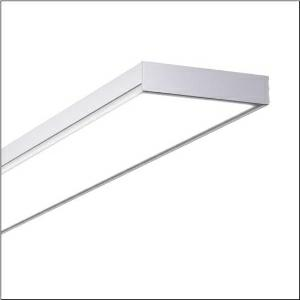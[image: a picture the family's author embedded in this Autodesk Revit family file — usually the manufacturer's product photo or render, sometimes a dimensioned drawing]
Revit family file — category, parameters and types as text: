
# Revit family: apollon_r__31_51mp25wm2341e_431d
name_source: partatom
category: Lighting Fixtures
units: mm (PartAtom-declared; Revit-internal decimal feet)

## family parameters
Cut with Voids When Loaded = No
Host = Face
Light Source = No
Part Type = Normal
Room Calculation Point = No
Round Connector Dimension = Use Diameter
Shared = No

## types (1)
- Apollon® 31 (1 x LED, 3600 lm, 27 W, 3000K)
    Apparent Load = 27 VA
    CIE Flux Codes = 61 87 97 97 100
    Color Rendering = 80
    Color Temperature = 3000K
    Default Elevation = 1800 mm
    Description = Apollon® 31, office luminaire, primary optical cover: micro prismatic cover, of PMMA, light emission: direct distribution, primary light characteristic: symmetric, installation type: surface-mounted, LED, rated luminous flux: 3.600lm, luminous efficacy: 132lm/W, light colour: 830, colour temperature: 3000K, control gear: ECG Multilumen, with terminal, 3-pole, mains connection: 220..240V, AC, 50/60Hz, rated input power: 27W, housing, of sheet steel, coil coated, metallic grey (RAL 9006), length: 1.245mm, width: 200mm, height: 44mm, protection rating (complete): IP20, insulation class (complete): insulation class II (safety insulation), certification: CE, impact resistance: IK02, permissible operating ambient temperature: -20..+40°C, packaging unit: 1 piece
    Height = 44 mm
    Lamp = 1 x LED
    Lamp Light Flux = 3600 lm
    Lamp Power = 27 W
    Lamp count = 1
    Length = 1245 mm
    Luminous efficacy = 133 lm/W
    Manufacturer = Siteco
    ModVariant = No
    Model = 51MP25WM2341E
    Mounting Place = Ceiling
    Mounting Type = Surface mounted
    Number of Poles = 1
    OnlyDefault = Yes
    Power Factor = 1
    Product Name = Apollon® 31
    Product group = office luminaire | ceiling mounted
    ProductGroupID = 302
    Protection Class = Protection class II
    Protection Degree = IP 20
    RLX_Detail_Level = 1
    RlxData = <blob elided: 24061 chars, md5=640a8a9e>
    Socket = socket
    Standby Power = 0 W
    System Light Flux = 3600 lm
    System Power = 27 W
    Type Comments = Product without accessories
    Type Image = l_1007091.jpg
    URL = http://relux.com
    VarID = ---
    Voltage = 0 V
    Weight = 0.00 kg
    Width = 200 mm  [stored 0.656168 ft]

note: [stored X ft] marks values corroborated as IEEE doubles in the binary element streams (Revit-internal decimal feet)

## geometry (parser evidence)
native form markers: Blend x4, Sweep x10
no freeform markers — native parametric forms only
